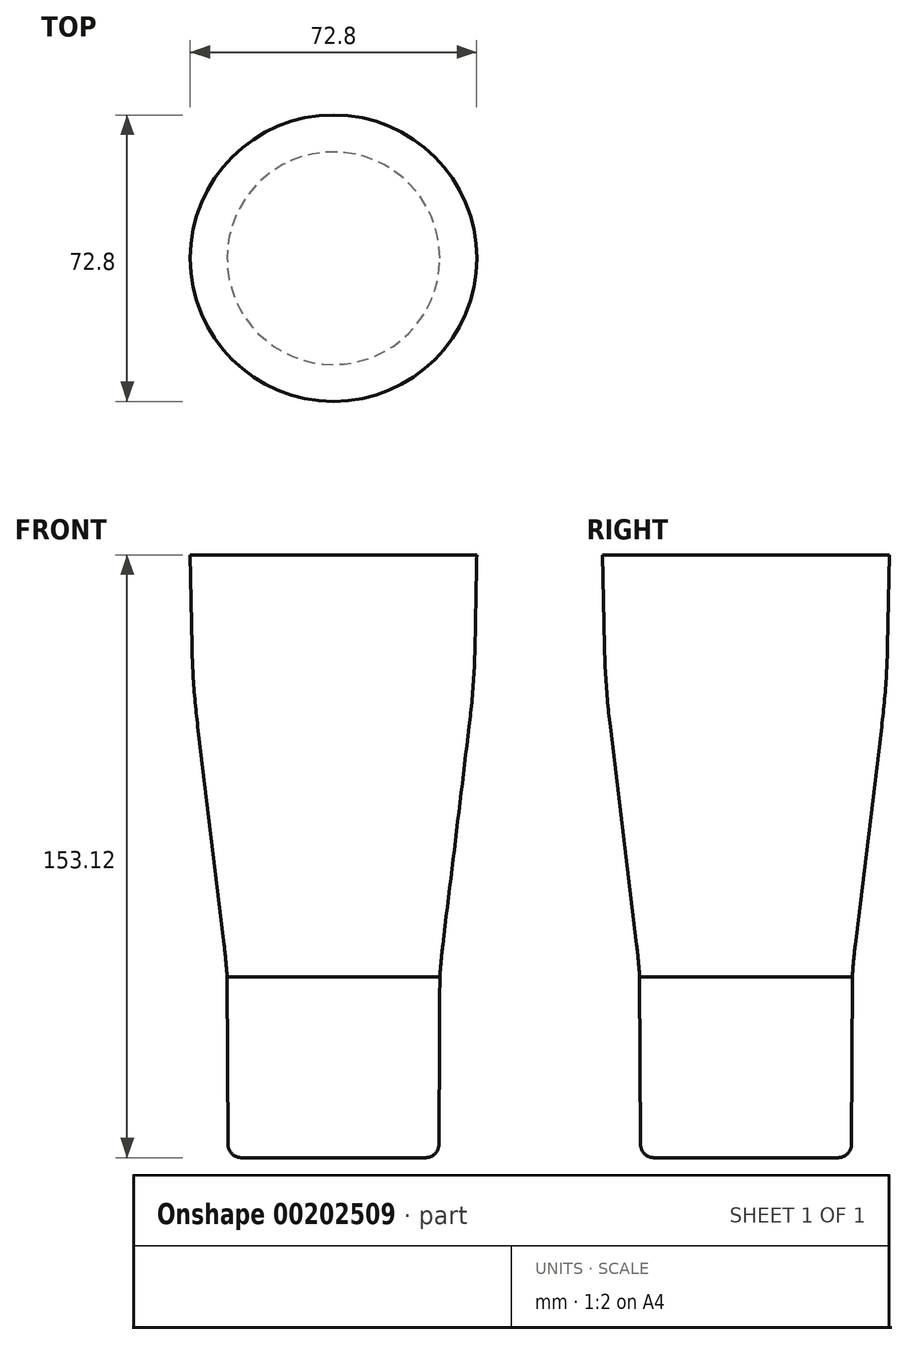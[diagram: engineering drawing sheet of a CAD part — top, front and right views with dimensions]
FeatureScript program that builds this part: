
annotation { "Feature Type Name" : "Feature", "Feature Type Description" : "" }
export const myFeature = defineFeature(function(context is Context, id is Id, definition is map)
    precondition{}
    {
        {
            var Q0;
            Q0=qCreatedBy(makeId("Front.planeOp"),FACE);
            var sketch = newSketch(context, id + "F0", { "sketchPlane" : qUnion([Q0])});
            skLineSegment(sketch, "E0", {"start": v(-0.04, -71.74) * mm, "end": v(-23.35, -71.74) * mm});
            skLineSegment(sketch, "E1", {"start": v(-0.04, 81.38) * mm, "end": v(-0.04, -71.74) * mm});
            skLineSegment(sketch, "E2", {"start": v(-27.05, -25.87) * mm, "end": v(-26.85, -68.27) * mm});
            skLineSegment(sketch, "E3", {"start": v(-36, 58.12) * mm, "end": v(-36.44, 81.38) * mm});
            skLineSegment(sketch, "E4", {"start": v(-27.81, -17.67) * mm, "end": v(-34.52, 37.77) * mm});
            skArc(sketch, "E5", {"start": v(-27.05, -25.87) * mm, "mid": v(-27.38, -21.76) * mm, "end": v(-27.81, -17.67) * mm});
            skArc(sketch, "E6", {"start": v(-36, 58.12) * mm, "mid": v(-35.5, 47.93) * mm, "end": v(-34.52, 37.77) * mm});
            skPoint(sketch, "E7.visualSharp", {"position": v(-26.83, -71.74) * mm});
            skArc(sketch, "E7.filletArc", {"start": v(-26.85, -68.27) * mm, "mid": v(-25.82, -70.73) * mm, "end": v(-23.35, -71.74) * mm});
            skPoint(sketch, "E8.start.orphan", {"position": v(-0.04, -73.74) * mm});
            skLineSegment(sketch, "E9", {"start": v(-36.44, 81.38) * mm, "end": v(-0.04, 81.38) * mm});
            skPoint(sketch, "E10.end.orphan", {"position": v(9.14, 81.38) * mm});
            skSolve(sketch);
        }
        {
            var Q0;
            Q0=makeQuery(id+"F0.imprint","IMPRINT",FACE,{"disambiguationData":[TD([[makeQuery(id+"F0.imprint","IMPRINT",EDGE,{"derivedFrom":sQuery(id+"F0.wireOp",EDGE,"E0")}),-1.0]])]});
            var Q1;
            Q1=sQuery(id+"F0.wireOp",EDGE,"E1");
            revolve(context, id + "F1", {"entities" : qUnion([Q0]), "axis" : qUnion([Q1]), "revolveType" : RevolveType.FULL});
        }
    });
